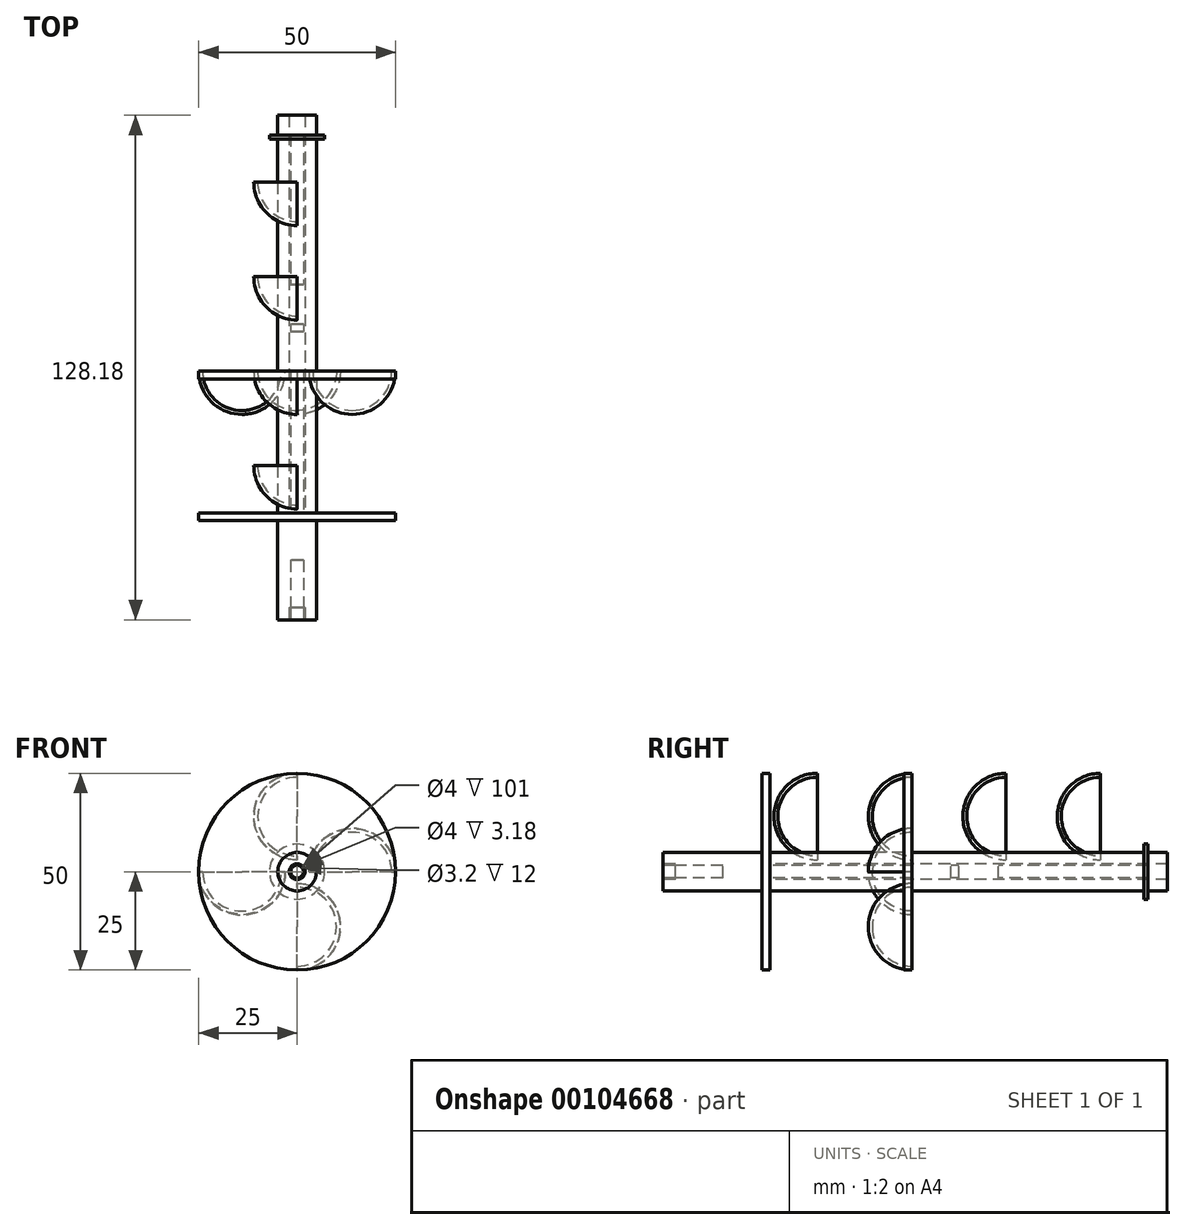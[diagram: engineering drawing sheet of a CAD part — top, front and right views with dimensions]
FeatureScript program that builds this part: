
annotation { "Feature Type Name" : "Feature", "Feature Type Description" : "" }
export const myFeature = defineFeature(function(context is Context, id is Id, definition is map)
    precondition{}
    {
        {
            var Q0;
            Q0=qCreatedBy(makeId("Right.planeOp"),FACE);
            var sketch = newSketch(context, id + "F0", { "sketchPlane" : qUnion([Q0])});
            skArc(sketch, "E0", {"start": v(0, 10) * mm, "mid": v(-7.07, 7.07) * mm, "end": v(-10, 0) * mm});
            skLineSegment(sketch, "E1", {"start": v(-10, 0) * mm, "end": v(0, 0) * mm});
            skLineSegment(sketch, "E2", {"start": v(0, 10) * mm, "end": v(0, 0) * mm});
            skArc(sketch, "E3", {"start": v(0, 11) * mm, "mid": v(-7.78, 7.78) * mm, "end": v(-11, 0) * mm});
            skLineSegment(sketch, "E4", {"start": v(0, 10) * mm, "end": v(0, 11) * mm});
            skLineSegment(sketch, "E5", {"start": v(-11, 0) * mm, "end": v(-10, 0) * mm});
            skSolve(sketch);
        }
        {
            var Q0;
            Q0=makeQuery(id+"F0.imprint","IMPRINT",FACE,{"disambiguationData":[TD([[makeQuery(id+"F0.imprint","IMPRINT",EDGE,{"derivedFrom":sQuery(id+"F0.wireOp",EDGE,"E0")}),-1.0]])]});
            var Q1;
            Q1=sQuery(id+"F0.wireOp",EDGE,"E0");
            var Q2;
            Q2=sQuery(id+"F0.wireOp",EDGE,"E1");
            revolve(context, id + "F1", {"entities" : qUnion([Q0]), "surfaceEntities" : qUnion([Q1]), "axis" : qUnion([Q2]), "revolveType" : RevolveType.TWO_DIRECTIONS, "angle" : 90 * degree, "angleBack" : 270 * degree});
        }
        {
            var Q0;
            Q0=makeQuery(id+"F1.opRevolve","SWEPT_BODY",BODY,{"disambiguationData":[OSD([sQuery(id+"F0.wireOp",EDGE,"E0"),sQuery(id+"F0.wireOp",EDGE,"E3"),sQuery(id+"F0.wireOp",EDGE,"E4"),sQuery(id+"F0.wireOp",EDGE,"E5")])]});
            transform(context, id + "F2", {"entities" : qUnion([Q0]), "transformType" : TransformType.TRANSLATION_3D, "dx" : 14 * mm, "dy" : 0 * mm, "dz" : 0 * mm, "makeCopy" : false});
        }
        {
            var Q0;
            Q0=qCreatedBy(makeId("Right.planeOp"),FACE);
            var sketch = newSketch(context, id + "F3", { "sketchPlane" : qUnion([Q0])});
            skLineSegment(sketch, "E6", {"start": v(-12, 0) * mm, "end": v(0, 0) * mm});
            skLineSegment(sketch, "E7", {"start": v(0, 0) * mm, "end": v(10, 0) * mm});
            skLineSegment(sketch, "E8", {"start": v(0, 0) * mm, "end": v(0, 25) * mm});
            skLineSegment(sketch, "E9.bottom", {"start": v(-2, 0) * mm, "end": v(0, 0) * mm});
            skLineSegment(sketch, "E9.top", {"start": v(-2, 25) * mm, "end": v(0, 25) * mm});
            skLineSegment(sketch, "E9.right", {"start": v(-2, 0) * mm, "end": v(-2, 25) * mm});
            skLineSegment(sketch, "E10", {"start": v(-24, 4.9) * mm, "end": v(0, 4.9) * mm});
            skLineSegment(sketch, "E11", {"start": v(0, 4.9) * mm, "end": v(10, 4.9) * mm});
            skLineSegment(sketch, "E12", {"start": v(-2, 4.9) * mm, "end": v(-2, 0) * mm});
            skLineSegment(sketch, "E13", {"start": v(0, 4.9) * mm, "end": v(0, 0) * mm});
            skLineSegment(sketch, "E14", {"start": v(22, 0) * mm, "end": v(34, 0) * mm});
            skLineSegment(sketch, "E15", {"start": v(34, 0) * mm, "end": v(46, 0) * mm});
            skLineSegment(sketch, "E16", {"start": v(-12, 0) * mm, "end": v(-24, 0) * mm});
            skLineSegment(sketch, "E17", {"start": v(-24, 0) * mm, "end": v(-36, 0) * mm});
            skLineSegment(sketch, "E18", {"start": v(-36, 0) * mm, "end": v(-48, 0) * mm});
            skLineSegment(sketch, "E19", {"start": v(10, 0) * mm, "end": v(22, 0) * mm});
            skLineSegment(sketch, "E20", {"start": v(-24, 4.9) * mm, "end": v(-24, 4.9) * mm});
            skLineSegment(sketch, "E21", {"start": v(10, 4.9) * mm, "end": v(22, 4.9) * mm});
            skLineSegment(sketch, "E22", {"start": v(-24, 4.9) * mm, "end": v(-36, 4.9) * mm});
            skLineSegment(sketch, "E23", {"start": v(-36, 0) * mm, "end": v(-36, 4.9) * mm});
            skLineSegment(sketch, "E24", {"start": v(46, 0) * mm, "end": v(65, 0) * mm});
            skLineSegment(sketch, "E25", {"start": v(65, 0) * mm, "end": v(77, 0) * mm});
            skLineSegment(sketch, "E26", {"start": v(-48, 0) * mm, "end": v(-60, 0) * mm});
            skLineSegment(sketch, "E27", {"start": v(-36, 0) * mm, "end": v(-36, 1.6) * mm});
            skLineSegment(sketch, "E28", {"start": v(-36, 1.6) * mm, "end": v(22, 1.6) * mm});
            skLineSegment(sketch, "E29", {"start": v(-36, 0) * mm, "end": v(-38, 0) * mm});
            skLineSegment(sketch, "E30", {"start": v(10, 4.9) * mm, "end": v(10, 0) * mm});
            skLineSegment(sketch, "E31", {"start": v(10, 0) * mm, "end": v(10, 25) * mm});
            skLineSegment(sketch, "E32", {"start": v(10, 25) * mm, "end": v(12, 25) * mm});
            skLineSegment(sketch, "E33", {"start": v(12, 25) * mm, "end": v(12, 0) * mm});
            skLineSegment(sketch, "E34", {"start": v(22, 0) * mm, "end": v(22, 25) * mm});
            skLineSegment(sketch, "E35", {"start": v(22, 25) * mm, "end": v(24, 25) * mm});
            skLineSegment(sketch, "E36", {"start": v(24, 25) * mm, "end": v(24, 0) * mm});
            skLineSegment(sketch, "E37", {"start": v(34, 0) * mm, "end": v(34, 25) * mm});
            skLineSegment(sketch, "E38", {"start": v(34, 25) * mm, "end": v(36, 25) * mm});
            skLineSegment(sketch, "E39", {"start": v(36, 25) * mm, "end": v(36, 0) * mm});
            skLineSegment(sketch, "E40", {"start": v(46, 0) * mm, "end": v(46, 25) * mm});
            skLineSegment(sketch, "E41", {"start": v(46, 25) * mm, "end": v(48, 25) * mm});
            skLineSegment(sketch, "E42", {"start": v(48, 25) * mm, "end": v(48, 0) * mm});
            skLineSegment(sketch, "E43", {"start": v(22, 4.9) * mm, "end": v(34, 4.9) * mm});
            skLineSegment(sketch, "E44", {"start": v(34, 4.9) * mm, "end": v(46, 4.9) * mm});
            skLineSegment(sketch, "E45", {"start": v(46, 4.9) * mm, "end": v(65, 4.9) * mm});
            skLineSegment(sketch, "E46", {"start": v(65, 4.9) * mm, "end": v(65, 0) * mm});
            skLineSegment(sketch, "E47", {"start": v(22, 1.6) * mm, "end": v(48, 1.6) * mm});
            skLineSegment(sketch, "E48", {"start": v(-12, 25) * mm, "end": v(-14, 25) * mm});
            skLineSegment(sketch, "E49", {"start": v(-14, 25) * mm, "end": v(-14, 0) * mm});
            skLineSegment(sketch, "E50", {"start": v(-24, 0) * mm, "end": v(-24, 25) * mm});
            skLineSegment(sketch, "E51", {"start": v(-24, 25) * mm, "end": v(-26, 25) * mm});
            skLineSegment(sketch, "E52", {"start": v(-26, 25) * mm, "end": v(-26, 0) * mm});
            skLineSegment(sketch, "E53", {"start": v(-36, 0) * mm, "end": v(-36, 25) * mm});
            skLineSegment(sketch, "E54", {"start": v(-36, 25) * mm, "end": v(-38, 25) * mm});
            skLineSegment(sketch, "E55", {"start": v(-38, 25) * mm, "end": v(-38, 0) * mm});
            skLineSegment(sketch, "E56", {"start": v(-36, 4.9) * mm, "end": v(-48, 4.9) * mm});
            skLineSegment(sketch, "E57", {"start": v(-48, 4.9) * mm, "end": v(-60, 4.9) * mm});
            skLineSegment(sketch, "E58", {"start": v(-60, 4.9) * mm, "end": v(-60, 0) * mm});
            skLineSegment(sketch, "E59", {"start": v(-36, 1.6) * mm, "end": v(-60, 1.6) * mm});
            skLineSegment(sketch, "E60", {"start": v(-60, 0) * mm, "end": v(-60, 1.6) * mm});
            skLineSegment(sketch, "E61", {"start": v(-2, 4.9) * mm, "end": v(0, 4.9) * mm});
            skLineSegment(sketch, "E62", {"start": v(0, 0) * mm, "end": v(-2, 0) * mm});
            skLineSegment(sketch, "E63", {"start": v(10, 0) * mm, "end": v(-2, 0) * mm});
            skLineSegment(sketch, "E64", {"start": v(10, 4.9) * mm, "end": v(-2, 4.9) * mm});
            skLineSegment(sketch, "E65", {"start": v(22, 1.6) * mm, "end": v(12, 1.6) * mm});
            skLineSegment(sketch, "E66", {"start": v(-2, 4.9) * mm, "end": v(10, 4.9) * mm});
            skLineSegment(sketch, "E67", {"start": v(-60, 4.9) * mm, "end": v(-63.18, 4.9) * mm});
            skLineSegment(sketch, "E68", {"start": v(-63.18, 4.9) * mm, "end": v(-63.18, 0) * mm});
            skLineSegment(sketch, "E69", {"start": v(-63.18, 0) * mm, "end": v(-60, 0) * mm});
            skLineSegment(sketch, "E70", {"start": v(-63.18, 0) * mm, "end": v(-63.18, 1.6) * mm});
            skLineSegment(sketch, "E71", {"start": v(60, 0) * mm, "end": v(60, 7) * mm});
            skLineSegment(sketch, "E72", {"start": v(60, 7) * mm, "end": v(59, 7) * mm});
            skLineSegment(sketch, "E73", {"start": v(59, 0) * mm, "end": v(59, 7) * mm});
            skLineSegment(sketch, "E74", {"start": v(-12, 25) * mm, "end": v(-12, 0) * mm});
            skPoint(sketch, "E75", {"position": v(65, 1.6) * mm});
            skLineSegment(sketch, "E76", {"start": v(48, 1.6) * mm, "end": v(65, 1.6) * mm});
            skLineSegment(sketch, "E77", {"start": v(65, 1.6) * mm, "end": v(65, 0) * mm});
            skLineSegment(sketch, "E78", {"start": v(-60, 1.6) * mm, "end": v(-63.18, 1.6) * mm});
            skLineSegment(sketch, "E79", {"start": v(-60, 0) * mm, "end": v(-38, 0) * mm});
            skLineSegment(sketch, "E80", {"start": v(-60, 4.9) * mm, "end": v(-36, 4.9) * mm});
            skLineSegment(sketch, "E81", {"start": v(-60, 0) * mm, "end": v(-36, 0) * mm});
            skLineSegment(sketch, "E82", {"start": v(-48, 4.9) * mm, "end": v(-48, 0) * mm});
            skLineSegment(sketch, "E83", {"start": v(-63.18, 2) * mm, "end": v(65, 2) * mm});
            skSolve(sketch);
        }
        {
            var Q0;
            {var subQ2=sQuery(id+"F3.wireOp",EDGE,"E69");Q0=makeQuery(id+"F3.imprint","IMPRINT",FACE,{"disambiguationData":[TD([[makeQuery(id+"F3.imprint","IMPRINT",EDGE,{"derivedFrom":subQ2}),1.0]])]});}
            var Q1;
            {var subQ3=sQuery(id+"F3.wireOp",EDGE,"E82");var subQ5=sQuery(id+"F3.wireOp",EDGE,"E81");var subQ6=makeQuery(id+"F3.imprint","INTERSECT",VERTEX,{"derivedFrom":[subQ5,subQ3]});Q1=makeQuery(id+"F3.imprint","IMPRINT",FACE,{"disambiguationData":[TD([[makeQuery(id+"F3.imprint","IMPRINT",EDGE,{"disambiguationData":[TD([[subQ6,1.0]])],"derivedFrom":subQ3}),-1.0]])]});}
            var Q2;
            {var subQ0=sQuery(id+"F3.wireOp",EDGE,"E81");var subQ1=sQuery(id+"F3.wireOp",EDGE,"E55");var subQ2=makeQuery(id+"F3.imprint","INTERSECT",VERTEX,{"derivedFrom":[subQ1,subQ0]});Q2=makeQuery(id+"F3.imprint","IMPRINT",FACE,{"disambiguationData":[TD([[makeQuery(id+"F3.imprint","IMPRINT",EDGE,{"disambiguationData":[TD([[subQ2,1.0]])],"derivedFrom":subQ1}),-1.0]])]});}
            var Q3;
            {var subQ0=sQuery(id+"F3.wireOp",EDGE,"E81");var subQ5=sQuery(id+"F3.wireOp",EDGE,"E55");var subQ6=makeQuery(id+"F3.imprint","INTERSECT",VERTEX,{"derivedFrom":[subQ5,subQ0]});Q3=makeQuery(id+"F3.imprint","IMPRINT",FACE,{"disambiguationData":[TD([[makeQuery(id+"F3.imprint","IMPRINT",EDGE,{"disambiguationData":[TD([[subQ6,1.0]])],"derivedFrom":subQ5}),1.0]])]});}
            var Q4;
            {var subQ1=sQuery(id+"F3.wireOp",EDGE,"E17");var subQ3=sQuery(id+"F3.wireOp",EDGE,"E52");var subQ4=makeQuery(id+"F3.imprint","INTERSECT",VERTEX,{"derivedFrom":[subQ1,subQ3]});Q4=makeQuery(id+"F3.imprint","IMPRINT",FACE,{"disambiguationData":[TD([[makeQuery(id+"F3.imprint","IMPRINT",EDGE,{"disambiguationData":[TD([[subQ4,1.0]])],"derivedFrom":subQ3}),-1.0]])]});}
            var Q5;
            {var subQ3=sQuery(id+"F3.wireOp",EDGE,"E52");var subQ5=sQuery(id+"F3.wireOp",EDGE,"E28");var subQ6=makeQuery(id+"F3.imprint","INTERSECT",VERTEX,{"derivedFrom":[subQ5,subQ3]});Q5=makeQuery(id+"F3.imprint","IMPRINT",FACE,{"disambiguationData":[TD([[makeQuery(id+"F3.imprint","IMPRINT",EDGE,{"disambiguationData":[TD([[subQ6,-1.0]])],"derivedFrom":subQ5}),-1.0]])]});}
            var Q6;
            {var subQ0=sQuery(id+"F3.wireOp",EDGE,"E50");var subQ5=sQuery(id+"F3.wireOp",EDGE,"E28");var subQ6=makeQuery(id+"F3.imprint","INTERSECT",VERTEX,{"derivedFrom":[subQ5,subQ0]});Q6=makeQuery(id+"F3.imprint","IMPRINT",FACE,{"disambiguationData":[TD([[makeQuery(id+"F3.imprint","IMPRINT",EDGE,{"disambiguationData":[TD([[subQ6,-1.0]])],"derivedFrom":subQ5}),-1.0]])]});}
            var Q7;
            {var subQ3=sQuery(id+"F3.wireOp",EDGE,"E49");var subQ5=sQuery(id+"F3.wireOp",EDGE,"E28");var subQ6=makeQuery(id+"F3.imprint","INTERSECT",VERTEX,{"derivedFrom":[subQ5,subQ3]});Q7=makeQuery(id+"F3.imprint","IMPRINT",FACE,{"disambiguationData":[TD([[makeQuery(id+"F3.imprint","IMPRINT",EDGE,{"disambiguationData":[TD([[subQ6,-1.0]])],"derivedFrom":subQ5}),-1.0]])]});}
            var Q8;
            {var subQ0=sQuery(id+"F3.wireOp",EDGE,"E6");Q8=makeQuery(id+"F3.imprint","IMPRINT",FACE,{"disambiguationData":[TD([[makeQuery(id+"F3.imprint","IMPRINT",EDGE,{"derivedFrom":subQ0}),1.0]])]});}
            var Q9;
            {var subQ0=sQuery(id+"F3.wireOp",EDGE,"E63");var subQ5=sQuery(id+"F3.wireOp",EDGE,"E13");var subQ6=makeQuery(id+"F3.imprint","INTERSECT",VERTEX,{"derivedFrom":[subQ5,subQ0]});Q9=makeQuery(id+"F3.imprint","IMPRINT",FACE,{"disambiguationData":[TD([[makeQuery(id+"F3.imprint","IMPRINT",EDGE,{"disambiguationData":[TD([[subQ6,1.0]])],"derivedFrom":subQ5}),-1.0]])]});}
            var Q10;
            {var subQ0=sQuery(id+"F3.wireOp",EDGE,"E63");var subQ1=sQuery(id+"F3.wireOp",EDGE,"E13");var subQ2=makeQuery(id+"F3.imprint","INTERSECT",VERTEX,{"derivedFrom":[subQ1,subQ0]});Q10=makeQuery(id+"F3.imprint","IMPRINT",FACE,{"disambiguationData":[TD([[makeQuery(id+"F3.imprint","IMPRINT",EDGE,{"disambiguationData":[TD([[subQ2,1.0]])],"derivedFrom":subQ1}),1.0]])]});}
            var Q11;
            {var subQ1=sQuery(id+"F3.wireOp",EDGE,"E19");var subQ3=sQuery(id+"F3.wireOp",EDGE,"E33");var subQ4=makeQuery(id+"F3.imprint","INTERSECT",VERTEX,{"derivedFrom":[subQ1,subQ3]});Q11=makeQuery(id+"F3.imprint","IMPRINT",FACE,{"disambiguationData":[TD([[makeQuery(id+"F3.imprint","IMPRINT",EDGE,{"disambiguationData":[TD([[subQ4,1.0]])],"derivedFrom":subQ1}),1.0]])]});}
            var Q12;
            {var subQ5=sQuery(id+"F3.wireOp",EDGE,"E65");Q12=makeQuery(id+"F3.imprint","IMPRINT",FACE,{"disambiguationData":[TD([[makeQuery(id+"F3.imprint","IMPRINT",EDGE,{"derivedFrom":subQ5}),1.0]])]});}
            var Q13;
            {var subQ1=sQuery(id+"F3.wireOp",EDGE,"E14");var subQ3=sQuery(id+"F3.wireOp",EDGE,"E36");var subQ4=makeQuery(id+"F3.imprint","INTERSECT",VERTEX,{"derivedFrom":[subQ1,subQ3]});Q13=makeQuery(id+"F3.imprint","IMPRINT",FACE,{"disambiguationData":[TD([[makeQuery(id+"F3.imprint","IMPRINT",EDGE,{"disambiguationData":[TD([[subQ4,1.0]])],"derivedFrom":subQ3}),-1.0]])]});}
            var Q14;
            {var subQ1=sQuery(id+"F3.wireOp",EDGE,"E14");var subQ3=sQuery(id+"F3.wireOp",EDGE,"E36");var subQ4=makeQuery(id+"F3.imprint","INTERSECT",VERTEX,{"derivedFrom":[subQ1,subQ3]});Q14=makeQuery(id+"F3.imprint","IMPRINT",FACE,{"disambiguationData":[TD([[makeQuery(id+"F3.imprint","IMPRINT",EDGE,{"disambiguationData":[TD([[subQ4,1.0]])],"derivedFrom":subQ3}),1.0]])]});}
            var Q15;
            {var subQ1=sQuery(id+"F3.wireOp",EDGE,"E15");var subQ3=sQuery(id+"F3.wireOp",EDGE,"E39");var subQ4=makeQuery(id+"F3.imprint","INTERSECT",VERTEX,{"derivedFrom":[subQ1,subQ3]});Q15=makeQuery(id+"F3.imprint","IMPRINT",FACE,{"disambiguationData":[TD([[makeQuery(id+"F3.imprint","IMPRINT",EDGE,{"disambiguationData":[TD([[subQ4,1.0]])],"derivedFrom":subQ3}),-1.0]])]});}
            var Q16;
            {var subQ1=sQuery(id+"F3.wireOp",EDGE,"E15");var subQ3=sQuery(id+"F3.wireOp",EDGE,"E39");var subQ4=makeQuery(id+"F3.imprint","INTERSECT",VERTEX,{"derivedFrom":[subQ1,subQ3]});Q16=makeQuery(id+"F3.imprint","IMPRINT",FACE,{"disambiguationData":[TD([[makeQuery(id+"F3.imprint","IMPRINT",EDGE,{"disambiguationData":[TD([[subQ4,1.0]])],"derivedFrom":subQ3}),1.0]])]});}
            var Q17;
            {var subQ1=sQuery(id+"F3.wireOp",EDGE,"E24");var subQ3=sQuery(id+"F3.wireOp",EDGE,"E42");var subQ4=makeQuery(id+"F3.imprint","INTERSECT",VERTEX,{"derivedFrom":[subQ1,subQ3]});Q17=makeQuery(id+"F3.imprint","IMPRINT",FACE,{"disambiguationData":[TD([[makeQuery(id+"F3.imprint","IMPRINT",EDGE,{"disambiguationData":[TD([[subQ4,1.0]])],"derivedFrom":subQ1}),1.0]])]});}
            var Q18;
            {var subQ0=sQuery(id+"F3.wireOp",EDGE,"E42");var subQ1=sQuery(id+"F3.wireOp",EDGE,"E24");var subQ2=makeQuery(id+"F3.imprint","INTERSECT",VERTEX,{"derivedFrom":[subQ1,subQ0]});Q18=makeQuery(id+"F3.imprint","IMPRINT",FACE,{"disambiguationData":[TD([[makeQuery(id+"F3.imprint","IMPRINT",EDGE,{"disambiguationData":[TD([[subQ2,-1.0]])],"derivedFrom":subQ1}),1.0]])]});}
            var Q19;
            {var subQ0=sQuery(id+"F3.wireOp",EDGE,"E77");Q19=makeQuery(id+"F3.imprint","IMPRINT",FACE,{"disambiguationData":[TD([[makeQuery(id+"F3.imprint","IMPRINT",EDGE,{"derivedFrom":subQ0}),-1.0]])]});}
            var Q20;
            {var subQ0=sQuery(id+"F3.wireOp",EDGE,"E71");var subQ1=sQuery(id+"F3.wireOp",EDGE,"E24");var subQ2=makeQuery(id+"F3.imprint","INTERSECT",VERTEX,{"derivedFrom":[subQ1,subQ0]});Q20=makeQuery(id+"F3.imprint","IMPRINT",FACE,{"disambiguationData":[TD([[makeQuery(id+"F3.imprint","IMPRINT",EDGE,{"disambiguationData":[TD([[subQ2,1.0]])],"derivedFrom":subQ1}),1.0]])]});}
            var Q21;
            {var subQ0=sQuery(id+"F3.wireOp",EDGE,"E73");var subQ1=sQuery(id+"F3.wireOp",EDGE,"E45");var subQ2=makeQuery(id+"F3.imprint","INTERSECT",VERTEX,{"derivedFrom":[subQ1,subQ0]});Q21=makeQuery(id+"F3.imprint","IMPRINT",FACE,{"disambiguationData":[TD([[makeQuery(id+"F3.imprint","IMPRINT",EDGE,{"disambiguationData":[TD([[subQ2,-1.0]])],"derivedFrom":subQ1}),-1.0]])]});}
            var Q22;
            {var subQ5=sQuery(id+"F3.wireOp",EDGE,"E72");Q22=makeQuery(id+"F3.imprint","IMPRINT",FACE,{"disambiguationData":[TD([[makeQuery(id+"F3.imprint","IMPRINT",EDGE,{"derivedFrom":subQ5}),1.0]])]});}
            var Q23;
            {var subQ1=sQuery(id+"F3.wireOp",EDGE,"E12");var subQ3=sQuery(id+"F3.wireOp",EDGE,"E83");var subQ4=makeQuery(id+"F3.imprint","INTERSECT",VERTEX,{"derivedFrom":[subQ1,subQ3]});Q23=makeQuery(id+"F3.imprint","IMPRINT",FACE,{"disambiguationData":[TD([[makeQuery(id+"F3.imprint","IMPRINT",EDGE,{"disambiguationData":[TD([[subQ4,-1.0]])],"derivedFrom":subQ3}),1.0]])]});}
            var Q24;
            Q24=makeQuery(id+"F3.imprint","IMPRINT",FACE,{"disambiguationData":[TD([[makeQuery(id+"F3.imprint","IMPRINT",EDGE,{"derivedFrom":sQuery(id+"F3.wireOp",EDGE,"E9.top")}),-1.0]])]});
            var Q25;
            Q25=sQuery(id+"F3.wireOp",EDGE,"E6");
            revolve(context, id + "F4", {"entities" : qUnion([Q0, Q1, Q2, Q3, Q4, Q5, Q6, Q7, Q8, Q9, Q10, Q11, Q12, Q13, Q14, Q15, Q16, Q17, Q18, Q19, Q20, Q21, Q22, Q23, Q24]), "axis" : qUnion([Q25]), "revolveType" : RevolveType.FULL});
        }
        {
            var Q0;
            Q0=makeQuery(id+"F1.opRevolve","SWEPT_BODY",BODY,{"disambiguationData":[OSD([sQuery(id+"F0.wireOp",EDGE,"E0"),sQuery(id+"F0.wireOp",EDGE,"E3"),sQuery(id+"F0.wireOp",EDGE,"E4"),sQuery(id+"F0.wireOp",EDGE,"E5")])]});
            var Q1;
            Q1=sQuery(id+"F3.wireOp",EDGE,"E6");
            transform(context, id + "F5", {"entities" : qUnion([Q0]), "transformType" : TransformType.ROTATION, "transformAxis" : qUnion([Q1]), "angle" : 90 * degree, "makeCopy" : true});
        }
        {
            var Q0;
            Q0=makeQuery(id+"F1.opRevolve","SWEPT_BODY",BODY,{"disambiguationData":[OSD([sQuery(id+"F0.wireOp",EDGE,"E0"),sQuery(id+"F0.wireOp",EDGE,"E3"),sQuery(id+"F0.wireOp",EDGE,"E4"),sQuery(id+"F0.wireOp",EDGE,"E5")])]});
            var Q1;
            Q1=makeQuery(id+"F5.opPattern","COPY",BODY,{"derivedFrom":makeQuery(id+"F1.opRevolve","SWEPT_BODY",BODY,{"disambiguationData":[OSD([sQuery(id+"F0.wireOp",EDGE,"E0"),sQuery(id+"F0.wireOp",EDGE,"E3"),sQuery(id+"F0.wireOp",EDGE,"E4"),sQuery(id+"F0.wireOp",EDGE,"E5")])]}),"instanceName":"1"});
            var Q2;
            Q2=sQuery(id+"F3.wireOp",EDGE,"E7");
            transform(context, id + "F6", {"entities" : qUnion([Q0, Q1]), "transformType" : TransformType.ROTATION, "transformAxis" : qUnion([Q2]), "angle" : 180 * degree, "makeCopy" : true});
        }
        {
            var Q0;
            Q0=makeQuery(id+"F6.opPattern","COPY",BODY,{"derivedFrom":makeQuery(id+"F5.opPattern","COPY",BODY,{"derivedFrom":makeQuery(id+"F1.opRevolve","SWEPT_BODY",BODY,{"disambiguationData":[OSD([sQuery(id+"F0.wireOp",EDGE,"E0"),sQuery(id+"F0.wireOp",EDGE,"E3"),sQuery(id+"F0.wireOp",EDGE,"E4"),sQuery(id+"F0.wireOp",EDGE,"E5")])]}),"instanceName":"1"}),"instanceName":"1"});
            var Q1;
            Q1=sQuery(id+"F3.wireOp",VERTEX,"E8.start");
            var Q2;
            Q2=sQuery(id+"F3.wireOp",VERTEX,"E17.start");
            transform(context, id + "F7", {"entities" : qUnion([Q0]), "transformType" : TransformType.TRANSLATION_ENTITY, "oppositeDirectionEntity" : false, "transformLine" : qUnion([Q1, Q2]), "makeCopy" : true});
        }
        {
            var Q0;
            Q0=makeQuery(id+"F7.opPattern","COPY",BODY,{"derivedFrom":makeQuery(id+"F6.opPattern","COPY",BODY,{"derivedFrom":makeQuery(id+"F5.opPattern","COPY",BODY,{"derivedFrom":makeQuery(id+"F1.opRevolve","SWEPT_BODY",BODY,{"disambiguationData":[OSD([sQuery(id+"F0.wireOp",EDGE,"E0"),sQuery(id+"F0.wireOp",EDGE,"E3"),sQuery(id+"F0.wireOp",EDGE,"E4"),sQuery(id+"F0.wireOp",EDGE,"E5")])]}),"instanceName":"1"}),"instanceName":"1"}),"instanceName":"1"});
            var Q1;
            Q1=makeQuery(id+"F6.opPattern","COPY",BODY,{"derivedFrom":makeQuery(id+"F5.opPattern","COPY",BODY,{"derivedFrom":makeQuery(id+"F1.opRevolve","SWEPT_BODY",BODY,{"disambiguationData":[OSD([sQuery(id+"F0.wireOp",EDGE,"E0"),sQuery(id+"F0.wireOp",EDGE,"E3"),sQuery(id+"F0.wireOp",EDGE,"E4"),sQuery(id+"F0.wireOp",EDGE,"E5")])]}),"instanceName":"1"}),"instanceName":"1"});
            var Q2;
            Q2=sQuery(id+"F3.wireOp",VERTEX,"E8.start");
            var Q3;
            Q3=sQuery(id+"F3.wireOp",VERTEX,"E42.end");
            transform(context, id + "F8", {"entities" : qUnion([Q0, Q1]), "transformType" : TransformType.TRANSLATION_ENTITY, "oppositeDirectionEntity" : false, "transformLine" : qUnion([Q2, Q3]), "makeCopy" : true});
        }
    });
